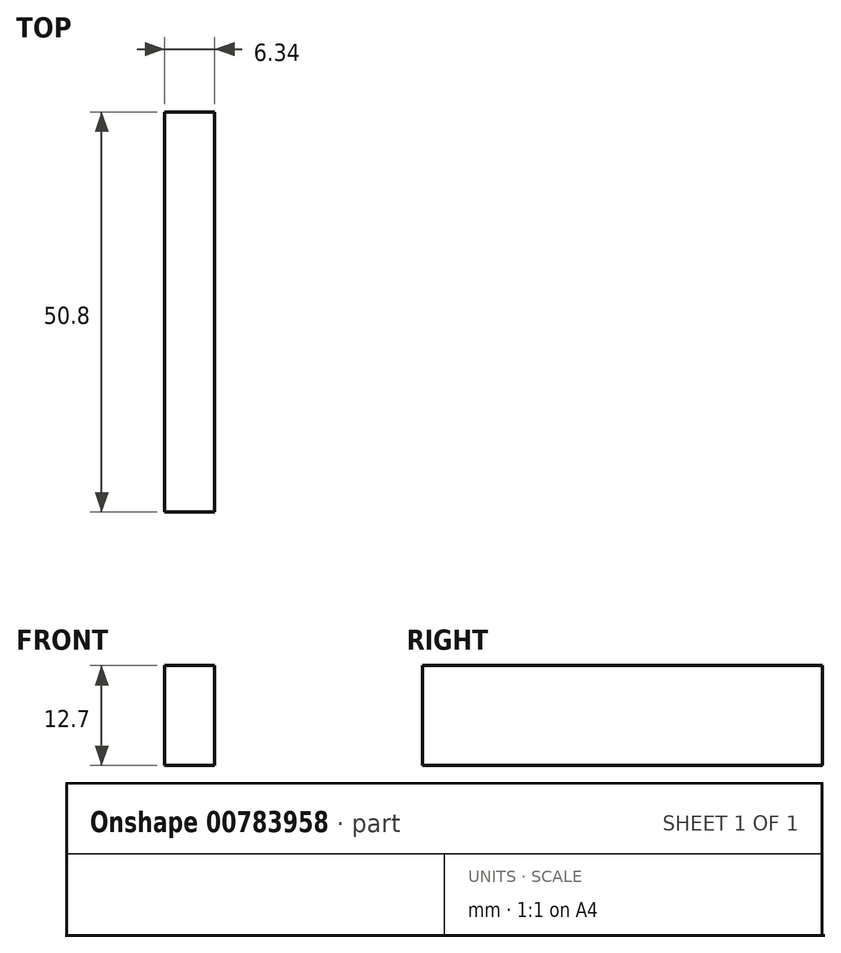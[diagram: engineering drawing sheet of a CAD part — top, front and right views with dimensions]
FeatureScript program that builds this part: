
annotation { "Feature Type Name" : "Feature", "Feature Type Description" : "" }
export const myFeature = defineFeature(function(context is Context, id is Id, definition is map)
    precondition{}
    {
        {
            var Q0;
            Q0=qCreatedBy(makeId("Top.planeOp"),FACE);
            var sketch = newSketch(context, id + "F0", { "sketchPlane" : qUnion([Q0])});
            skLineSegment(sketch, "E0", {"start": v(-3.17, 18.78) * mm, "end": v(-3.18, 69.58) * mm});
            skLineSegment(sketch, "E1", {"start": v(-3.18, 69.58) * mm, "end": v(3.18, 69.58) * mm});
            skLineSegment(sketch, "E2", {"start": v(3.17, 69.58) * mm, "end": v(3.18, 18.78) * mm});
            skLineSegment(sketch, "E3", {"start": v(-3.18, 69.58) * mm, "end": v(0, 69.58) * mm});
            skLineSegment(sketch, "E4", {"start": v(-3.17, 18.78) * mm, "end": v(3.17, 18.78) * mm});
            skSolve(sketch);
        }
        {
            var Q0;
            Q0 = qSketchRegion(id + "F0", true);
            extrude(context, id + "F1", {"entities" : qUnion([Q0]), "depth" : 12.7 * mm, "offsetDistance" : 25.4 * mm});
        }
    });
